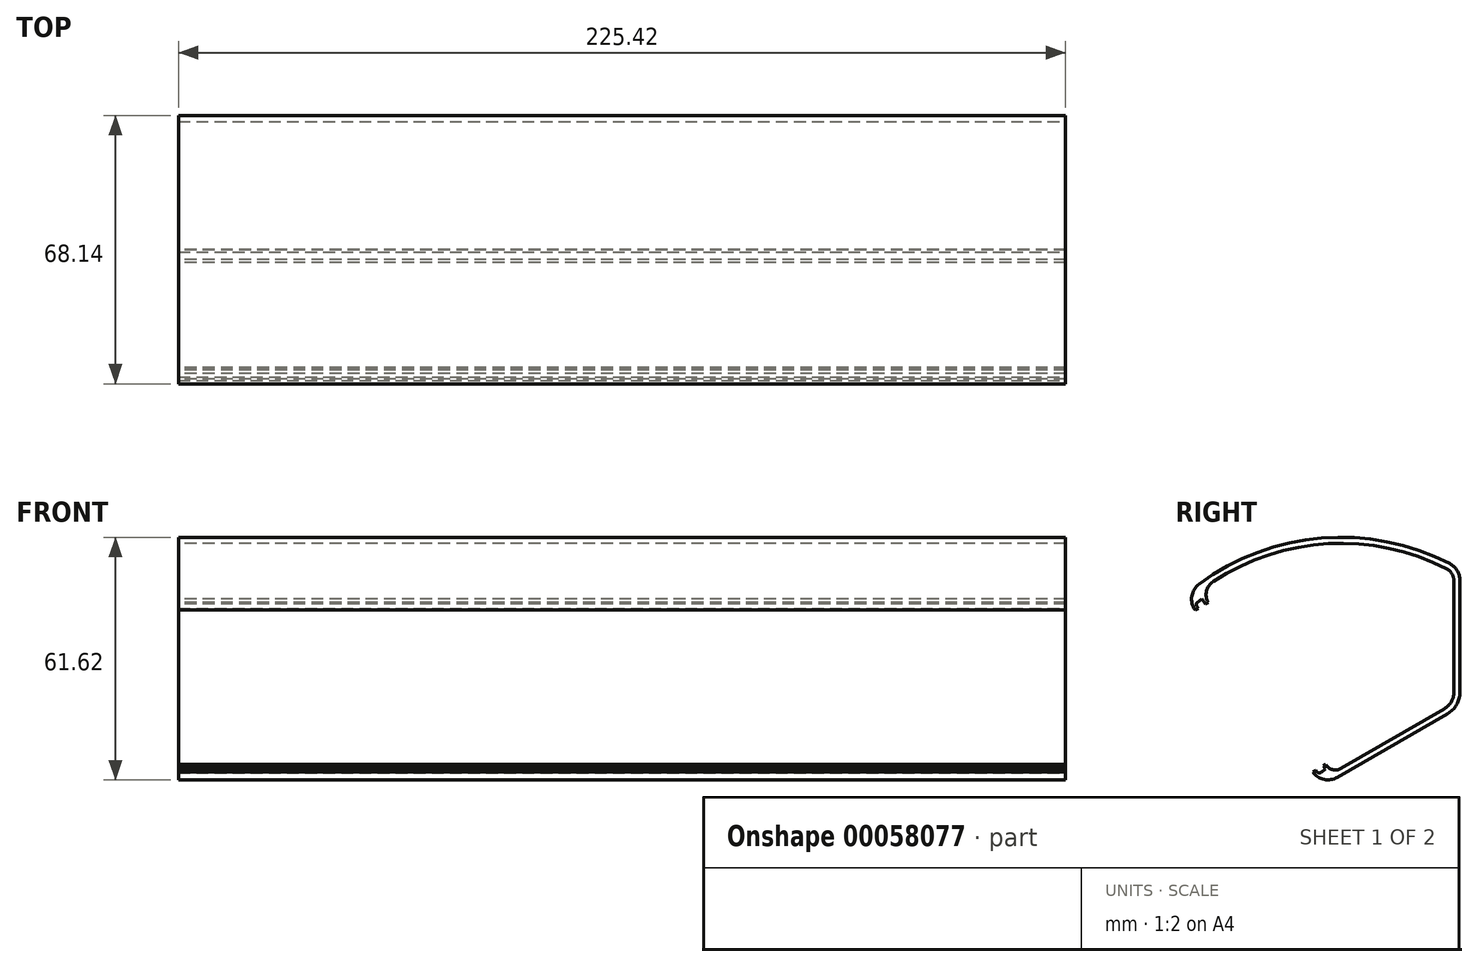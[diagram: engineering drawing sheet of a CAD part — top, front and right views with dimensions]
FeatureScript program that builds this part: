
annotation { "Feature Type Name" : "Feature", "Feature Type Description" : "" }
export const myFeature = defineFeature(function(context is Context, id is Id, definition is map)
    precondition{}
    {
        {
            var Q0;
            Q0=qCreatedBy(makeId("Right.planeOp"),FACE);
            var sketch = newSketch(context, id + "F0", { "sketchPlane" : qUnion([Q0])});
            skLineSegment(sketch, "E0", {"start": v(-30.25, -17.46) * mm, "end": v(0, 0) * mm});
            skLineSegment(sketch, "E1", {"start": v(0, 0) * mm, "end": v(0, 34.93) * mm});
            skArc(sketch, "E2", {"start": v(0, 34.92) * mm, "mid": v(-30.25, 43.03) * mm, "end": v(-60.5, 34.92) * mm});
            skLineSegment(sketch, "E3", {"start": v(0, 34.93) * mm, "end": v(-30.25, -17.46) * mm, "construction": true});
            skPoint(sketch, "E4", {"position": v(-15.12, 8.73) * mm});
            skLineSegment(sketch, "E5", {"start": v(0, 0) * mm, "end": v(-60.5, 34.93) * mm, "construction": true});
            skArc(sketch, "E6", {"start": v(-60.5, 34.92) * mm, "mid": v(-52.39, 4.68) * mm, "end": v(-30.25, -17.46) * mm, "construction": true});
            skLineSegment(sketch, "E7", {"start": v(0, 34.93) * mm, "end": v(-60.5, 34.92) * mm, "construction": true});
            skLineSegment(sketch, "E8", {"start": v(-63.08, 18.83) * mm, "end": v(-34.8, -20.1) * mm, "construction": true});
            skPoint(sketch, "E9.endSnap0", {"position": v(-48.94, -0.63) * mm});
            skLineSegment(sketch, "E10", {"start": v(0, 0) * mm, "end": v(-63.08, 18.83) * mm, "construction": true});
            skLineSegment(sketch, "E11", {"start": v(0, 0) * mm, "end": v(-34.8, -20.1) * mm, "construction": true});
            skLineSegment(sketch, "E12", {"start": v(-34.8, -20.1) * mm, "end": v(-69.9, 28.22) * mm});
            skLineSegment(sketch, "E13", {"start": v(-30.25, -17.46) * mm, "end": v(-34.8, -20.1) * mm});
            skArc(sketch, "E14", {"start": v(-60.5, 34.92) * mm, "mid": v(-65.36, 31.8) * mm, "end": v(-69.9, 28.22) * mm});
            skSolve(sketch);
        }
        {
            var Q0;
            Q0=qSketchRegion(id+"F0",true);
            extrude(context, id + "F1", {"entities" : qUnion([Q0]), "endBound" : BoundingType.SYMMETRIC, "depth" : 225.42 * mm});
        }
        {
            var Q0;
            Q0=makeQuery(id+"F1.opExtrude","SWEPT_EDGE",EDGE,{"disambiguationData":[OSD([sQuery(id+"F0.wireOp",EDGE,"E1"),sQuery(id+"F0.wireOp",EDGE,"E2")])]});
            var Q1;
            Q1=makeQuery(id+"F1.opExtrude","SWEPT_EDGE",EDGE,{"disambiguationData":[OSD([sQuery(id+"F0.wireOp",EDGE,"E12"),sQuery(id+"F0.wireOp",EDGE,"E14")])]});
            var Q2;
            Q2=makeQuery(id+"F1.opExtrude","SWEPT_EDGE",EDGE,{"disambiguationData":[OSD([sQuery(id+"F0.wireOp",EDGE,"E12"),sQuery(id+"F0.wireOp",EDGE,"E13")])]});
            fillet(context, id + "F2", {"entities" : qUnion([Q0, Q1, Q2]), "radius" : 4.76 * mm, "tangentPropagation" : true, "allowEdgeOverflow" : false});
        }
        {
            var Q0;
            Q0=makeQuery(id+"F1.opExtrude","SWEPT_EDGE",EDGE,{"disambiguationData":[OSD([sQuery(id+"F0.wireOp",EDGE,"E0"),sQuery(id+"F0.wireOp",EDGE,"E1")])]});
            fillet(context, id + "F3", {"entities" : qUnion([Q0]), "radius" : 6.35 * mm, "tangentPropagation" : true, "allowEdgeOverflow" : false});
        }
        {
            var Q0;
            Q0=makeQuery(id+"F1.opExtrude","CAP_FACE",FACE,{"disambiguationData":[OSD([sQuery(id+"F0.wireOp",EDGE,"E0"),sQuery(id+"F0.wireOp",EDGE,"E1"),sQuery(id+"F0.wireOp",EDGE,"E2"),sQuery(id+"F0.wireOp",EDGE,"E12"),sQuery(id+"F0.wireOp",EDGE,"E13"),sQuery(id+"F0.wireOp",EDGE,"E14")])],"isStart":true});
            var Q1;
            Q1=makeQuery(id+"F1.opExtrude","CAP_FACE",FACE,{"disambiguationData":[OSD([sQuery(id+"F0.wireOp",EDGE,"E0"),sQuery(id+"F0.wireOp",EDGE,"E1"),sQuery(id+"F0.wireOp",EDGE,"E2"),sQuery(id+"F0.wireOp",EDGE,"E12"),sQuery(id+"F0.wireOp",EDGE,"E13"),sQuery(id+"F0.wireOp",EDGE,"E14")])],"isStart":false});
            shell(context, id + "F4", {"entities" : qUnion([Q0, Q1]), "thickness" : 1.52 * mm});
        }
        {
            var Q0;
            Q0=makeQuery(id+"F1.opExtrude","CAP_FACE",FACE,{"disambiguationData":[OSD([sQuery(id+"F0.wireOp",EDGE,"E0"),sQuery(id+"F0.wireOp",EDGE,"E1"),sQuery(id+"F0.wireOp",EDGE,"E2"),sQuery(id+"F0.wireOp",EDGE,"E12"),sQuery(id+"F0.wireOp",EDGE,"E13"),sQuery(id+"F0.wireOp",EDGE,"E14")])],"isStart":true});
            var sketch = newSketch(context, id + "F5", { "sketchPlane" : qUnion([Q0])});
            skLineSegment(sketch, "E15", {"start": v(36, -15.86) * mm, "end": v(37.32, -16.62) * mm});
            skLineSegment(sketch, "E16", {"start": v(37.32, -16.62) * mm, "end": v(67.23, 24.55) * mm});
            skLineSegment(sketch, "E17", {"start": v(67.23, 24.55) * mm, "end": v(65.9, 25.31) * mm});
            skLineSegment(sketch, "E18", {"start": v(65.9, 25.31) * mm, "end": v(36, -15.86) * mm});
            skSolve(sketch);
        }
        {
            var Q0;
            Q0 = qSketchRegion(id + "F5", true);
            var Q1;
            Q1=makeQuery(id+"F1.opExtrude","CAP_FACE",FACE,{"disambiguationData":[OSD([sQuery(id+"F0.wireOp",EDGE,"E0"),sQuery(id+"F0.wireOp",EDGE,"E1"),sQuery(id+"F0.wireOp",EDGE,"E2"),sQuery(id+"F0.wireOp",EDGE,"E12"),sQuery(id+"F0.wireOp",EDGE,"E13"),sQuery(id+"F0.wireOp",EDGE,"E14")])],"isStart":false});
            extrude(context, id + "F6", {"entities" : qUnion([Q0]), "operationType" : NewBodyOperationType.REMOVE, "endBound" : BoundingType.UP_TO_SURFACE, "oppositeDirection" : true, "endBoundEntityFace" : qUnion([Q1]), "depth" : 25.4 * mm});
        }
        {
            var Q0;
            Q0=makeQuery(id+"F1.opExtrude","CAP_FACE",FACE,{"disambiguationData":[OSD([sQuery(id+"F0.wireOp",EDGE,"E0"),sQuery(id+"F0.wireOp",EDGE,"E1"),sQuery(id+"F0.wireOp",EDGE,"E2"),sQuery(id+"F0.wireOp",EDGE,"E12"),sQuery(id+"F0.wireOp",EDGE,"E13"),sQuery(id+"F0.wireOp",EDGE,"E14")])],"isStart":true});
            var sketch = newSketch(context, id + "F7", { "sketchPlane" : qUnion([Q0])});
            skLineSegment(sketch, "E19", {"start": v(65.9, 25.31) * mm, "end": v(63.93, 26.45) * mm});
            skArc(sketch, "E20", {"start": v(63.93, 26.45) * mm, "mid": v(64.36, 29.37) * mm, "end": v(62.67, 31.8) * mm});
            skLineSegment(sketch, "E21", {"start": v(63.93, 26.45) * mm, "end": v(65.73, 29.57) * mm, "construction": true});
            skArc(sketch, "E22", {"start": v(30.28, -15.72) * mm, "mid": v(32.36, -16) * mm, "end": v(34.02, -14.72) * mm});
            skLineSegment(sketch, "E23", {"start": v(34.02, -14.72) * mm, "end": v(32.72, -16.97) * mm, "construction": true});
            skLineSegment(sketch, "E24", {"start": v(34.02, -14.72) * mm, "end": v(36, -15.86) * mm});
            skSolve(sketch);
        }
        {
            var Q0;
            Q0=makeQuery(id+"F7.imprint","IMPRINT",FACE,{"disambiguationData":[TD([[makeQuery(id+"F7.imprint","IMPRINT",EDGE,{"derivedFrom":sQuery(id+"F7.wireOp",EDGE,"E19")}),-1.0]])]});
            var Q1;
            {var subQ0=sQuery(id+"F7.wireOp",EDGE,"E22");Q1=makeQuery(id+"F7.imprint","IMPRINT",FACE,{"disambiguationData":[TD([[makeQuery(id+"F7.imprint","IMPRINT",EDGE,{"derivedFrom":subQ0}),-1.0]])]});}
            var Q2;
            Q2=makeQuery(id+"F1.opExtrude","CAP_FACE",FACE,{"disambiguationData":[OSD([sQuery(id+"F0.wireOp",EDGE,"E0"),sQuery(id+"F0.wireOp",EDGE,"E1"),sQuery(id+"F0.wireOp",EDGE,"E2"),sQuery(id+"F0.wireOp",EDGE,"E12"),sQuery(id+"F0.wireOp",EDGE,"E13"),sQuery(id+"F0.wireOp",EDGE,"E14")])],"isStart":false});
            extrude(context, id + "F8", {"entities" : qUnion([Q0, Q1]), "operationType" : NewBodyOperationType.ADD, "endBound" : BoundingType.UP_TO_SURFACE, "oppositeDirection" : true, "endBoundEntityFace" : qUnion([Q2]), "depth" : 25.4 * mm});
        }
        {
            var Q0;
            {var subQ0=sQuery(id+"F0.wireOp",EDGE,"E14");var subQ1=sQuery(id+"F0.wireOp",EDGE,"E13");var subQ2=sQuery(id+"F0.wireOp",EDGE,"E12");var subQ3=sQuery(id+"F0.wireOp",EDGE,"E2");var subQ4=sQuery(id+"F0.wireOp",EDGE,"E1");var subQ5=sQuery(id+"F0.wireOp",EDGE,"E0");Q0=makeQuery(id+"FeprFQKJkuQr1AW_1.boolean.opBoolean","MERGE",FACE,{"derivedFrom":[makeQuery(id+"F1.opExtrude","CAP_FACE",FACE,{"disambiguationData":[OSD([subQ5,subQ4,subQ3,subQ2,subQ1,subQ0])],"isStart":true}),makeQuery(id+"FeprFQKJkuQr1AW_1.opExtrude","CAP_FACE",FACE,{"disambiguationData":[OSD([subQ5,subQ4,subQ3,subQ2,subQ1,subQ0,sQuery(id+"F7.wireOp",EDGE,"E19"),sQuery(id+"F7.wireOp",EDGE,"E20")])],"isStart":true}),makeQuery(id+"FeprFQKJkuQr1AW_1.opExtrude","CAP_FACE",FACE,{"disambiguationData":[OSD([subQ5,subQ4,subQ3,subQ2,subQ1,subQ0,sQuery(id+"F7.wireOp",EDGE,"XGq2ZlwC-Ggzm-sTt0-k8ZL-KJ8AWHBd69yi"),sQuery(id+"F7.wireOp",EDGE,"E22")])],"isStart":true})]});}
            var sketch = newSketch(context, id + "F9", { "sketchPlane" : qUnion([Q0])});
            skLineSegment(sketch, "E25", {"start": v(65.51, 27.37) * mm, "end": v(67.26, 26.1) * mm});
            skLineSegment(sketch, "E26", {"start": v(65.51, 27.37) * mm, "end": v(34.1, -15.86) * mm});
            skLineSegment(sketch, "E27", {"start": v(35.85, -17.13) * mm, "end": v(67.26, 26.1) * mm});
            skLineSegment(sketch, "E28", {"start": v(67.23, 24.55) * mm, "end": v(37.32, -16.62) * mm, "construction": true});
            skLineSegment(sketch, "E29", {"start": v(34.1, -15.86) * mm, "end": v(35.85, -17.13) * mm});
            skSolve(sketch);
        }
        {
            var Q0;
            Q0 = qSketchRegion(id + "F9", true);
            var Q1;
            {var subQ0=sQuery(id+"F0.wireOp",EDGE,"E14");var subQ1=sQuery(id+"F0.wireOp",EDGE,"E13");var subQ2=sQuery(id+"F0.wireOp",EDGE,"E12");var subQ3=sQuery(id+"F0.wireOp",EDGE,"E2");var subQ4=sQuery(id+"F0.wireOp",EDGE,"E1");var subQ5=sQuery(id+"F0.wireOp",EDGE,"E0");Q1=makeQuery(id+"F8.boolean.opBoolean","MERGE",FACE,{"derivedFrom":[makeQuery(id+"F1.opExtrude","CAP_FACE",FACE,{"disambiguationData":[OSD([subQ5,subQ4,subQ3,subQ2,subQ1,subQ0])],"isStart":false}),makeQuery(id+"F8.opExtrude","CAP_FACE",FACE,{"disambiguationData":[OSD([subQ5,subQ4,subQ3,subQ2,subQ1,subQ0,sQuery(id+"F7.wireOp",EDGE,"E19"),sQuery(id+"F7.wireOp",EDGE,"E20")])],"isStart":false}),makeQuery(id+"F8.opExtrude","CAP_FACE",FACE,{"disambiguationData":[OSD([subQ5,subQ4,subQ3,subQ2,subQ1,subQ0,sQuery(id+"F7.wireOp",EDGE,"E22"),sQuery(id+"F7.wireOp",EDGE,"E24")])],"isStart":false})]});}
            extrude(context, id + "F10", {"entities" : qUnion([Q0]), "operationType" : NewBodyOperationType.REMOVE, "endBound" : BoundingType.UP_TO_SURFACE, "oppositeDirection" : true, "endBoundEntityFace" : qUnion([Q1]), "depth" : 25.4 * mm});
        }
        {
            var Q0;
            Q0=makeQuery(id+"F10.boolean.opBoolean","COPY",EDGE,{"derivedFrom":makeQuery(id+"F10.opExtrude","SWEPT_EDGE",EDGE,{"disambiguationData":[OSD([sQuery(id+"F9.wireOp",EDGE,"E27"),sQuery(id+"F9.wireOp",EDGE,"E29")])]})});
            var Q1;
            Q1=makeQuery(id+"F10.boolean.opBoolean","COPY",EDGE,{"derivedFrom":makeQuery(id+"F10.opExtrude","SWEPT_EDGE",EDGE,{"disambiguationData":[OSD([sQuery(id+"F9.wireOp",EDGE,"E25"),sQuery(id+"F9.wireOp",EDGE,"E27")])]})});
            fillet(context, id + "F11", {"entities" : qUnion([Q0, Q1]), "radius" : 0.76 * mm, "tangentPropagation" : true, "allowEdgeOverflow" : false});
        }
    });
